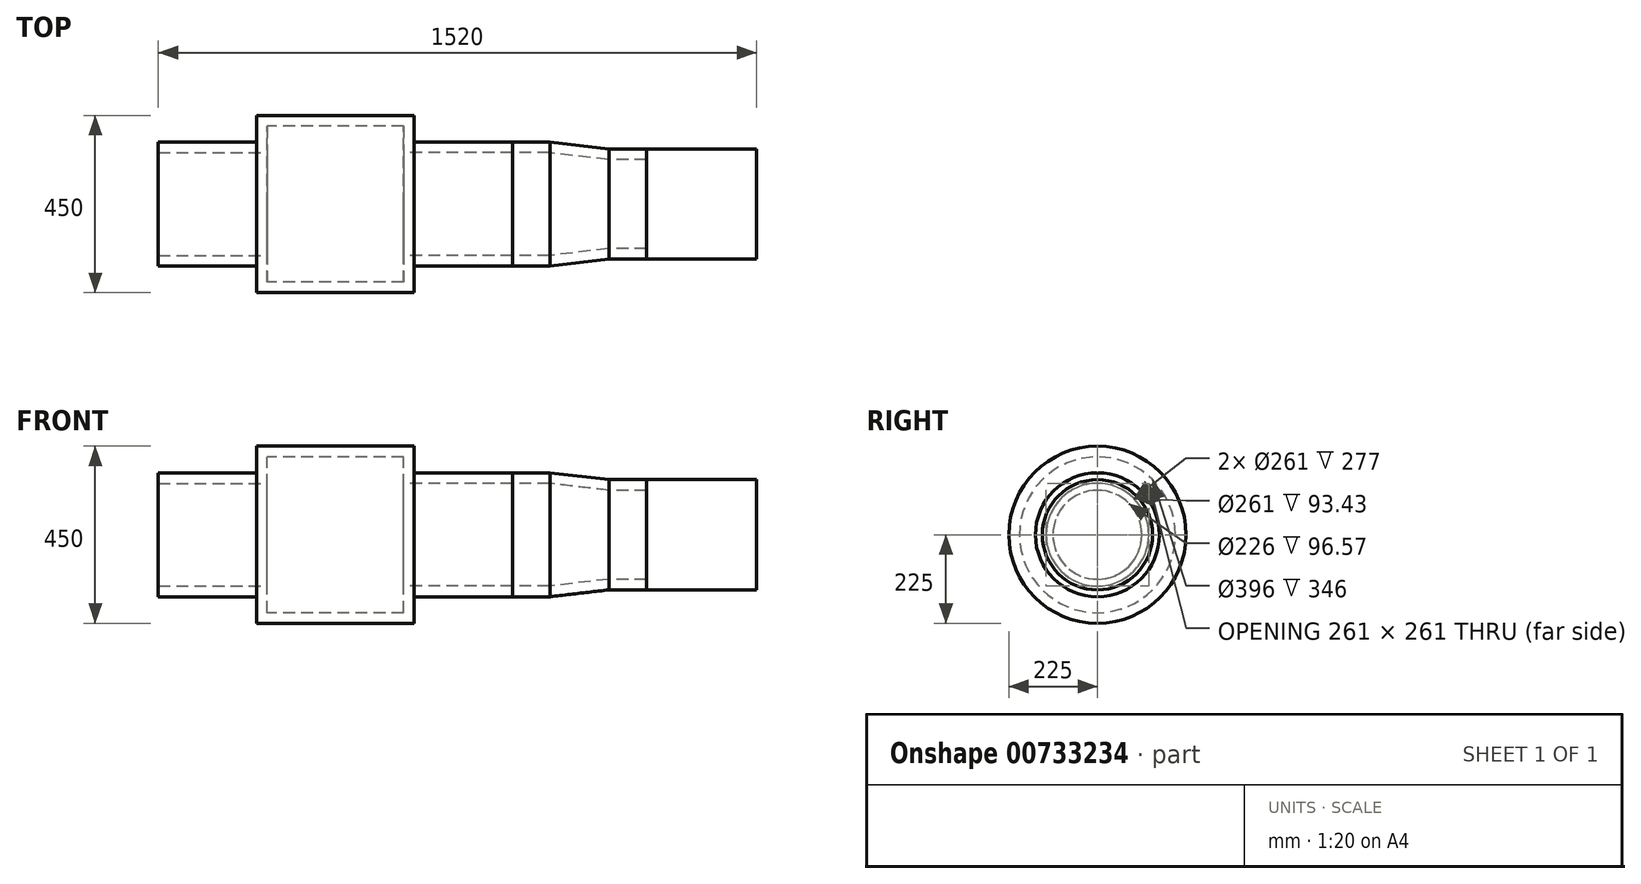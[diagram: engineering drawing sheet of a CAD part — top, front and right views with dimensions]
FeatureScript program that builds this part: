
annotation { "Feature Type Name" : "Feature", "Feature Type Description" : "" }
export const myFeature = defineFeature(function(context is Context, id is Id, definition is map)
    precondition{}
    {
        {
            var Q0;
            Q0=qCreatedBy(makeId("Right.planeOp"),FACE);
            var sketch = newSketch(context, id + "F0", { "sketchPlane" : qUnion([Q0])});
            skCircle(sketch, "E0", {"center": v(0, 0) * mm, "radius": 225 * mm});
            skSolve(sketch);
        }
        {
            var Q0;
            Q0 = qSketchRegion(id + "F0", true);
            extrude(context, id + "F1", {"entities" : qUnion([Q0]), "endBound" : BoundingType.SYMMETRIC, "depth" : 400 * mm, "offsetDistance" : 25 * mm});
        }
        {
            var Q0;
            Q0=makeQuery(id+"F1.opExtrude","CAP_FACE",FACE,{"disambiguationData":[OSD([sQuery(id+"F0.wireOp",EDGE,"E0")])],"isStart":false});
            var sketch = newSketch(context, id + "F2", { "sketchPlane" : qUnion([Q0])});
            skCircle(sketch, "E1", {"center": v(0, 0) * mm, "radius": 157.5 * mm});
            skSolve(sketch);
        }
        {
            var Q0;
            Q0 = qSketchRegion(id + "F2", true);
            extrude(context, id + "F3", {"entities" : qUnion([Q0]), "operationType" : NewBodyOperationType.ADD, "depth" : 250 * mm, "offsetDistance" : 25 * mm});
        }
        {
            var Q0;
            Q0=makeQuery(id+"F1.opExtrude","CAP_FACE",FACE,{"disambiguationData":[OSD([sQuery(id+"F0.wireOp",EDGE,"E0")])],"isStart":true});
            var sketch = newSketch(context, id + "F4", { "sketchPlane" : qUnion([Q0])});
            skCircle(sketch, "E2", {"center": v(0, 0) * mm, "radius": 157.5 * mm});
            skSolve(sketch);
        }
        {
            var Q0;
            Q0 = qSketchRegion(id + "F4", true);
            extrude(context, id + "F5", {"entities" : qUnion([Q0]), "operationType" : NewBodyOperationType.ADD, "depth" : 250 * mm, "offsetDistance" : 25 * mm});
        }
        {
            var Q0;
            Q0=makeQuery(id+"F3.opExtrude","CAP_FACE",FACE,{"disambiguationData":[OSD([sQuery(id+"F2.wireOp",EDGE,"E1")])],"isStart":false});
            var sketch = newSketch(context, id + "F6", { "sketchPlane" : qUnion([Q0])});
            skCircle(sketch, "E3", {"center": v(0, 0) * mm, "radius": 157.5 * mm});
            skSolve(sketch);
        }
        {
            var Q0;
            Q0 = qSketchRegion(id + "F6", true);
            extrude(context, id + "F7", {"entities" : qUnion([Q0]), "depth" : 95 * mm, "offsetDistance" : 25 * mm});
        }
        {
            var Q0;
            Q0=makeQuery(id+"F7.opExtrude","CAP_FACE",FACE,{"disambiguationData":[OSD([sQuery(id+"F6.wireOp",EDGE,"E3")])],"isStart":false});
            var sketch = newSketch(context, id + "F8", { "sketchPlane" : qUnion([Q0])});
            skCircle(sketch, "E4", {"center": v(0, 0) * mm, "radius": 157.5 * mm});
            skSolve(sketch);
        }
        {
            var Q0;
            Q0=makeQuery(id+"F8.imprint","IMPRINT",FACE,{"disambiguationData":[TD([[makeQuery(id+"F8.imprint","IMPRINT",EDGE,{"derivedFrom":sQuery(id+"F8.wireOp",EDGE,"E4")}),1.0]])]});
            cPlane(context, id + "F9", {"entities" : qUnion([Q0]), "cplaneType" : CPlaneType.OFFSET, "offset" : 150 * mm, "width" : 150 * mm, "height" : 150 * mm});
        }
        {
            var Q0;
            Q0=qCreatedBy(id+"F9.planeOp",FACE);
            var sketch = newSketch(context, id + "F10", { "sketchPlane" : qUnion([Q0])});
            skCircle(sketch, "E5", {"center": v(0, 0) * mm, "radius": 140 * mm});
            skSolve(sketch);
        }
        {
            var Q1;
            Q1 = qSketchRegion(id + "F8", true);
            var Q2;
            Q2 = qSketchRegion(id + "F10", true);
            loft(context, id + "F11", {"operationType" : NewBodyOperationType.ADD, "sheetProfilesArray" : [{ "sheetProfileEntities" : qUnion([Q1]) }, { "sheetProfileEntities" : qUnion([Q2]) }]});
        }
        {
            var Q0;
            Q0=makeQuery(id+"F11.opLoft","CAP_FACE",FACE,{"disambiguationData":[OSD([makeQuery(id+"F10.imprint","IMPRINT",FACE,{"disambiguationData":[TD([[makeQuery(id+"F10.imprint","IMPRINT",EDGE,{"derivedFrom":sQuery(id+"F10.wireOp",EDGE,"E5")}),1.0]])]})])],"isStart":true});
            var sketch = newSketch(context, id + "F12", { "sketchPlane" : qUnion([Q0])});
            skCircle(sketch, "E6", {"center": v(0, 0) * mm, "radius": 140 * mm});
            skSolve(sketch);
        }
        {
            var Q0;
            Q0 = qSketchRegion(id + "F12", true);
            extrude(context, id + "F13", {"entities" : qUnion([Q0]), "operationType" : NewBodyOperationType.ADD, "depth" : 95 * mm, "offsetDistance" : 25 * mm});
        }
        {
            var Q0;
            Q0=makeQuery(id+"F5.opExtrude","CAP_FACE",FACE,{"disambiguationData":[OSD([sQuery(id+"F4.wireOp",EDGE,"E2")])],"isStart":false});
            var Q1;
            Q1=makeQuery(id+"F3.opExtrude","CAP_FACE",FACE,{"disambiguationData":[OSD([sQuery(id+"F2.wireOp",EDGE,"E1")])],"isStart":false});
            shell(context, id + "F14", {"entities" : qUnion([Q0, Q1]), "thickness" : 27 * mm});
        }
        {
            var Q0;
            Q0=makeQuery(id+"F13.opExtrude","CAP_FACE",FACE,{"disambiguationData":[OSD([sQuery(id+"F12.wireOp",EDGE,"E6")])],"isStart":false});
            var Q1;
            Q1=makeQuery(id+"F7.opExtrude","CAP_FACE",FACE,{"disambiguationData":[OSD([sQuery(id+"F6.wireOp",EDGE,"E3")])],"isStart":true});
            shell(context, id + "F15", {"entities" : qUnion([Q0, Q1]), "thickness" : 27 * mm});
        }
        {
            var Q0;
            Q0=makeQuery(id+"F13.opExtrude","CAP_FACE",FACE,{"disambiguationData":[OSD([sQuery(id+"F12.wireOp",EDGE,"E6")])],"isStart":false});
            var sketch = newSketch(context, id + "F16", { "sketchPlane" : qUnion([Q0])});
            skCircle(sketch, "E7", {"center": v(0, 0) * mm, "radius": 140 * mm});
            skSolve(sketch);
        }
        {
            var Q0;
            Q0 = qSketchRegion(id + "F16", true);
            extrude(context, id + "F17", {"entities" : qUnion([Q0]), "depth" : 280 * mm, "offsetDistance" : 25 * mm});
        }
    });
